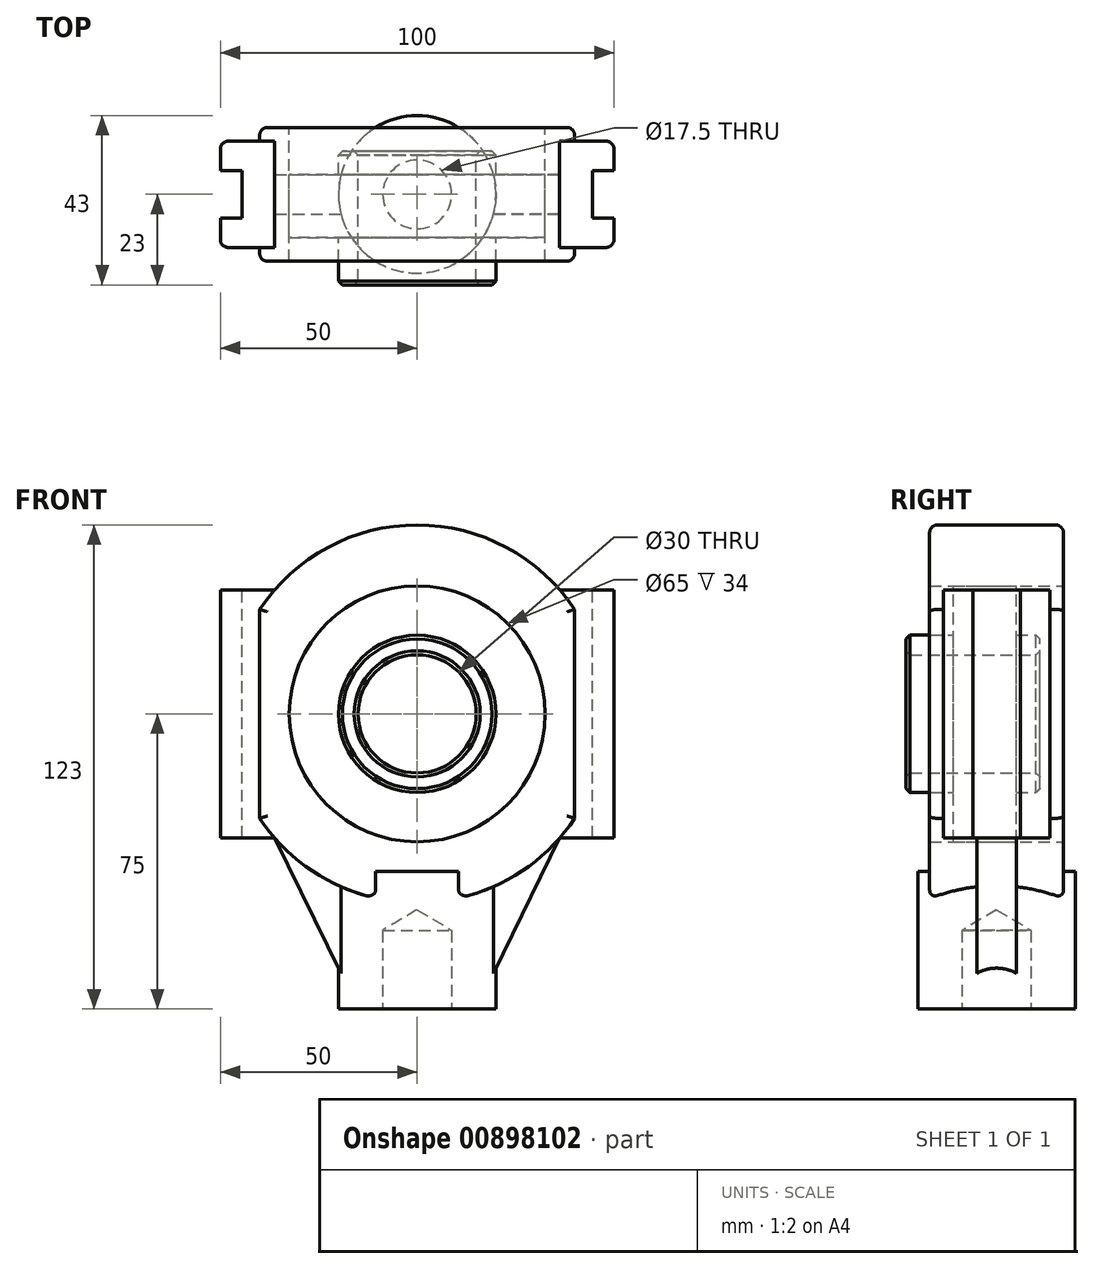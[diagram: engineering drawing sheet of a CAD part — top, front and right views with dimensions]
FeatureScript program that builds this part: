
annotation { "Feature Type Name" : "Feature", "Feature Type Description" : "" }
export const myFeature = defineFeature(function(context is Context, id is Id, definition is map)
    precondition{}
    {
        {
            var Q0;
            Q0=qCreatedBy(makeId("Front.planeOp"),FACE);
            var sketch = newSketch(context, id + "F0", { "sketchPlane" : qUnion([Q0])});
            skArc(sketch, "E0", {"start": v(-40, -26.53) * mm, "mid": v(0, -48) * mm, "end": v(40, -26.53) * mm});
            skLineSegment(sketch, "E1.left", {"start": v(-40, 26.53) * mm, "end": v(-40, -26.53) * mm});
            skLineSegment(sketch, "E1.right", {"start": v(40, 26.53) * mm, "end": v(40, -26.53) * mm});
            skArc(sketch, "E2.trimOffspring", {"start": v(40, 26.53) * mm, "mid": v(0, 48) * mm, "end": v(-40, 26.53) * mm});
            skCircle(sketch, "E3", {"center": v(0, 0) * mm, "radius": 32.5 * mm});
            skSolve(sketch);
        }
        {
            var Q0;
            Q0=qSketchRegion(id+"F0",true);
            extrude(context, id + "F1", {"entities" : qUnion([Q0]), "endBound" : BoundingType.SYMMETRIC, "depth" : 34 * mm, "offsetDistance" : 25 * mm});
        }
        {
            var Q0;
            Q0=qCreatedBy(makeId("Front.planeOp"),FACE);
            var sketch = newSketch(context, id + "F2", { "sketchPlane" : qUnion([Q0])});
            skLineSegment(sketch, "E4.bottom", {"start": v(-50, 31.5) * mm, "end": v(-36.22, 31.5) * mm});
            skLineSegment(sketch, "E4.top", {"start": v(-50, -31.5) * mm, "end": v(-36.22, -31.5) * mm});
            skLineSegment(sketch, "E4.left", {"start": v(-50, 31.5) * mm, "end": v(-50, -31.5) * mm});
            skLineSegment(sketch, "E4.right", {"start": v(-36.22, 31.5) * mm, "end": v(-36.22, -31.5) * mm});
            skPoint(sketch, "E4.middle", {"position": v(-43.1, 0) * mm});
            skLineSegment(sketch, "E5.bottom", {"start": v(36.22, 31.5) * mm, "end": v(50, 31.5) * mm});
            skLineSegment(sketch, "E5.top", {"start": v(36.22, -31.5) * mm, "end": v(50, -31.5) * mm});
            skLineSegment(sketch, "E5.left", {"start": v(36.22, 31.5) * mm, "end": v(36.22, -31.5) * mm});
            skLineSegment(sketch, "E5.right", {"start": v(50, 31.5) * mm, "end": v(50, -31.5) * mm});
            skPoint(sketch, "E5.middle", {"position": v(43.1, 0) * mm});
            skSolve(sketch);
        }
        {
            var Q0;
            Q0=qSketchRegion(id+"F2",true);
            extrude(context, id + "F3", {"entities" : qUnion([Q0]), "operationType" : NewBodyOperationType.ADD, "endBound" : BoundingType.SYMMETRIC, "depth" : 27 * mm, "offsetDistance" : 25 * mm});
        }
        {
            var Q0;
            Q0=makeQuery(id+"F3.opExtrude","SWEPT_FACE",FACE,{"disambiguationData":[OSD([sQuery(id+"F2.wireOp",EDGE,"E5.bottom")])]});
            var sketch = newSketch(context, id + "F4", { "sketchPlane" : qUnion([Q0])});
            skLineSegment(sketch, "E6.bottom", {"start": v(44.5, 6) * mm, "end": v(55.5, 6) * mm});
            skLineSegment(sketch, "E6.top", {"start": v(44.5, -6) * mm, "end": v(55.5, -6) * mm});
            skLineSegment(sketch, "E6.left", {"start": v(44.5, 6) * mm, "end": v(44.5, -6) * mm});
            skLineSegment(sketch, "E6.right", {"start": v(55.5, 6) * mm, "end": v(55.5, -6) * mm});
            skPoint(sketch, "E6.middle", {"position": v(50, 0) * mm});
            skLineSegment(sketch, "E7.bottom", {"start": v(-44.5, 6) * mm, "end": v(-55.5, 6) * mm});
            skLineSegment(sketch, "E7.top", {"start": v(-44.5, -6) * mm, "end": v(-55.5, -6) * mm});
            skLineSegment(sketch, "E7.left", {"start": v(-44.5, 6) * mm, "end": v(-44.5, -6) * mm});
            skLineSegment(sketch, "E7.right", {"start": v(-55.5, 6) * mm, "end": v(-55.5, -6) * mm});
            skPoint(sketch, "E7.middle", {"position": v(-50, 0) * mm});
            skSolve(sketch);
        }
        {
            var Q0;
            Q0=qSketchRegion(id+"F4",true);
            extrude(context, id + "F5", {"entities" : qUnion([Q0]), "operationType" : NewBodyOperationType.REMOVE, "endBound" : BoundingType.THROUGH_ALL, "oppositeDirection" : true, "depth" : 25 * mm, "offsetDistance" : 25 * mm});
        }
        {
            var Q0;
            Q0=qCreatedBy(makeId("Top.planeOp"),FACE);
            cPlane(context, id + "F6", {"entities" : qUnion([Q0]), "cplaneType" : CPlaneType.OFFSET, "offset" : 40 * mm, "oppositeDirection" : true, "width" : 150 * mm, "height" : 150 * mm});
        }
        {
            var Q0;
            Q0=qCreatedBy(id+"F6.planeOp",FACE);
            var sketch = newSketch(context, id + "F7", { "sketchPlane" : qUnion([Q0])});
            skCircle(sketch, "E8", {"center": v(0, 0) * mm, "radius": 20 * mm});
            skSolve(sketch);
        }
        {
            var Q0;
            Q0=qSketchRegion(id+"F7",true);
            extrude(context, id + "F8", {"entities" : qUnion([Q0]), "operationType" : NewBodyOperationType.ADD, "oppositeDirection" : true, "depth" : 35 * mm, "offsetDistance" : 25 * mm});
        }
        {
            var Q0;
            Q0=makeQuery(id+"F8.opExtrude","CAP_FACE",FACE,{"disambiguationData":[OSD([sQuery(id+"F7.wireOp",EDGE,"E8")])],"isStart":false});
            var sketch = newSketch(context, id + "F9", { "sketchPlane" : qUnion([Q0])});
            skPoint(sketch, "E9", {"position": v(0, 0) * mm});
            skSolve(sketch);
        }
        {
            var Q0;
            Q0=sQuery(id+"F9.wireOp",VERTEX,"E9");
            var Q1;
            Q1=makeQuery(id+"F1.opExtrude","SWEPT_BODY",BODY,{"disambiguationData":[OSD([sQuery(id+"F0.wireOp",EDGE,"E0"),sQuery(id+"F0.wireOp",EDGE,"E1.left"),sQuery(id+"F0.wireOp",EDGE,"E1.right"),sQuery(id+"F0.wireOp",EDGE,"E2.trimOffspring"),sQuery(id+"F0.wireOp",EDGE,"E3")])]});
            hole(context, id + "F10", {"style" : HoleStyle.SIMPLE, "endStyle" : HoleEndStyle.BLIND, "standardTappedOrClearance" : lookupTablePath({ "fit" : "Normal", "standard" : "ISO", "size" : "M16", "type" : "Clearance" }), "standardBlindInLast" : lookupTablePath({ "fit" : "Normal", "standard" : "ISO", "size" : "M16", "type" : "Clearance" }), "holeDiameter" : 17.5 * mm, "majorDiameter" : 5 * mm, "holeDepth" : 20 * mm, "isTappedThrough" : true, "tappedDepth" : 12 * mm, "tapClearance" : 3, "startFromSketch" : true, "locations" : qUnion([Q0]), "scope" : qUnion([Q1])});
        }
        {
            var Q0;
            Q0=qCreatedBy(makeId("Front.planeOp"),FACE);
            var sketch = newSketch(context, id + "F11", { "sketchPlane" : qUnion([Q0])});
            skLineSegment(sketch, "E10", {"start": v(-36.22, -31.5) * mm, "end": v(-17.5, -69.7) * mm});
            skLineSegment(sketch, "E11", {"start": v(-17.5, -69.7) * mm, "end": v(-17.5, -44.7) * mm});
            skLineSegment(sketch, "E12", {"start": v(-17.5, -44.7) * mm, "end": v(-36.22, -31.5) * mm});
            skLineSegment(sketch, "E13", {"start": v(17.5, -44.7) * mm, "end": v(36.22, -31.5) * mm});
            skLineSegment(sketch, "E14", {"start": v(36.22, -31.5) * mm, "end": v(17.5, -69.7) * mm});
            skLineSegment(sketch, "E15", {"start": v(17.5, -69.7) * mm, "end": v(17.5, -44.7) * mm});
            skSolve(sketch);
        }
        {
            var Q0;
            Q0=qSketchRegion(id+"F11",true);
            extrude(context, id + "F12", {"entities" : qUnion([Q0]), "operationType" : NewBodyOperationType.ADD, "endBound" : BoundingType.SYMMETRIC, "depth" : 10 * mm, "offsetDistance" : 25 * mm});
        }
        {
            var Q0;
            Q0=qCreatedBy(makeId("Front.planeOp"),FACE);
            var sketch = newSketch(context, id + "F13", { "sketchPlane" : qUnion([Q0])});
            skCircle(sketch, "E16", {"center": v(0, 0) * mm, "radius": 32.5 * mm});
            skCircle(sketch, "E17", {"center": v(0, 0) * mm, "radius": 20 * mm});
            skSolve(sketch);
        }
        {
            var Q0;
            Q0=qSketchRegion(id+"F13",true);
            extrude(context, id + "F14", {"entities" : qUnion([Q0]), "depth" : 11 * mm, "offsetDistance" : 25 * mm, "hasSecondDirection" : true, "secondDirectionOppositeDirection" : true, "secondDirectionDepth" : 5 * mm});
        }
        {
            var Q0;
            Q0=qCreatedBy(makeId("Front.planeOp"),FACE);
            var sketch = newSketch(context, id + "F15", { "sketchPlane" : qUnion([Q0])});
            skCircle(sketch, "E18", {"center": v(0, 0) * mm, "radius": 15 * mm});
            skCircle(sketch, "E19", {"center": v(0, 0) * mm, "radius": 20 * mm});
            skSolve(sketch);
        }
        {
            var Q0;
            Q0=qSketchRegion(id+"F15",true);
            extrude(context, id + "F16", {"entities" : qUnion([Q0]), "operationType" : NewBodyOperationType.ADD, "depth" : 23 * mm, "offsetDistance" : 25 * mm, "hasSecondDirection" : true, "secondDirectionOppositeDirection" : true, "secondDirectionDepth" : 11 * mm});
        }
        {
            var Q0;
            Q0=makeQuery(id+"F16.opExtrude","CAP_FACE",FACE,{"disambiguationData":[OSD([sQuery(id+"F15.wireOp",EDGE,"E18"),sQuery(id+"F15.wireOp",EDGE,"E19")])],"isStart":false});
            var Q1;
            Q1=makeQuery(id+"F16.opExtrude","CAP_FACE",FACE,{"disambiguationData":[OSD([sQuery(id+"F15.wireOp",EDGE,"E18"),sQuery(id+"F15.wireOp",EDGE,"E19")])],"isStart":true});
            chamfer(context, id + "F17", {"entities" : qUnion([Q0, Q1]), "width" : 1 * mm, "tangentPropagation" : true});
        }
        {
            var Q0;
            Q0=makeQuery(id+"F1.opExtrude","CAP_EDGE",EDGE,{"disambiguationData":[OSD([sQuery(id+"F0.wireOp",EDGE,"E2.trimOffspring")])],"isStart":false});
            var Q1;
            {var subQ0=sQuery(id+"F0.wireOp",EDGE,"E0");var subQ1=sQuery(id+"F0.wireOp",EDGE,"E1.left");Q1=makeQuery(id+"F8.boolean.opBoolean","SPLIT",EDGE,{"disambiguationData":[TD([makeQuery(id+"F1.opExtrude","SWEPT_FACE",FACE,{"disambiguationData":[OSD([subQ1])]})])],"derivedFrom":makeQuery(id+"F1.opExtrude","CAP_EDGE",EDGE,{"disambiguationData":[OSD([subQ0])],"isStart":false})});}
            var Q2;
            {var subQ0=sQuery(id+"F0.wireOp",EDGE,"E0");var subQ1=sQuery(id+"F0.wireOp",EDGE,"E1.right");Q2=makeQuery(id+"F8.boolean.opBoolean","SPLIT",EDGE,{"disambiguationData":[TD([makeQuery(id+"F1.opExtrude","SWEPT_FACE",FACE,{"disambiguationData":[OSD([subQ1])]})])],"derivedFrom":makeQuery(id+"F1.opExtrude","CAP_EDGE",EDGE,{"disambiguationData":[OSD([subQ0])],"isStart":false})});}
            var Q3;
            Q3=makeQuery(id+"F1.opExtrude","CAP_EDGE",EDGE,{"disambiguationData":[OSD([sQuery(id+"F0.wireOp",EDGE,"E1.left")])],"isStart":false});
            var Q4;
            Q4=makeQuery(id+"F1.opExtrude","CAP_EDGE",EDGE,{"disambiguationData":[OSD([sQuery(id+"F0.wireOp",EDGE,"E1.right")])],"isStart":false});
            var Q5;
            Q5=makeQuery(id+"F1.opExtrude","CAP_EDGE",EDGE,{"disambiguationData":[OSD([sQuery(id+"F0.wireOp",EDGE,"E2.trimOffspring")])],"isStart":true});
            var Q6;
            Q6=makeQuery(id+"F1.opExtrude","CAP_EDGE",EDGE,{"disambiguationData":[OSD([sQuery(id+"F0.wireOp",EDGE,"E1.right")])],"isStart":true});
            var Q7;
            {var subQ0=sQuery(id+"F0.wireOp",EDGE,"E0");var subQ1=sQuery(id+"F0.wireOp",EDGE,"E1.right");Q7=makeQuery(id+"F8.boolean.opBoolean","SPLIT",EDGE,{"disambiguationData":[TD([makeQuery(id+"F1.opExtrude","SWEPT_FACE",FACE,{"disambiguationData":[OSD([subQ1])]})])],"derivedFrom":makeQuery(id+"F1.opExtrude","CAP_EDGE",EDGE,{"disambiguationData":[OSD([subQ0])],"isStart":true})});}
            var Q8;
            {var subQ0=sQuery(id+"F0.wireOp",EDGE,"E0");var subQ1=sQuery(id+"F0.wireOp",EDGE,"E1.left");Q8=makeQuery(id+"F8.boolean.opBoolean","SPLIT",EDGE,{"disambiguationData":[TD([makeQuery(id+"F1.opExtrude","SWEPT_FACE",FACE,{"disambiguationData":[OSD([subQ1])]})])],"derivedFrom":makeQuery(id+"F1.opExtrude","CAP_EDGE",EDGE,{"disambiguationData":[OSD([subQ0])],"isStart":true})});}
            var Q9;
            Q9=makeQuery(id+"F1.opExtrude","CAP_EDGE",EDGE,{"disambiguationData":[OSD([sQuery(id+"F0.wireOp",EDGE,"E1.left")])],"isStart":true});
            var Q10;
            Q10=makeQuery(id+"F3.opExtrude","CAP_EDGE",EDGE,{"disambiguationData":[OSD([sQuery(id+"F2.wireOp",EDGE,"E5.right")])],"isStart":false});
            var Q11;
            Q11=makeQuery(id+"F3.opExtrude","CAP_EDGE",EDGE,{"disambiguationData":[OSD([sQuery(id+"F2.wireOp",EDGE,"E5.right")])],"isStart":true});
            var Q12;
            Q12=makeQuery(id+"F3.opExtrude","CAP_EDGE",EDGE,{"disambiguationData":[OSD([sQuery(id+"F2.wireOp",EDGE,"E4.left")])],"isStart":false});
            var Q13;
            Q13=makeQuery(id+"F3.opExtrude","CAP_EDGE",EDGE,{"disambiguationData":[OSD([sQuery(id+"F2.wireOp",EDGE,"E4.left")])],"isStart":true});
            fillet(context, id + "F18", {"entities" : qUnion([Q0, Q1, Q2, Q3, Q4, Q5, Q6, Q7, Q8, Q9, Q10, Q11, Q12, Q13]), "radius" : 2 * mm, "tangentPropagation" : true, "allowEdgeOverflow" : false});
        }
    });
